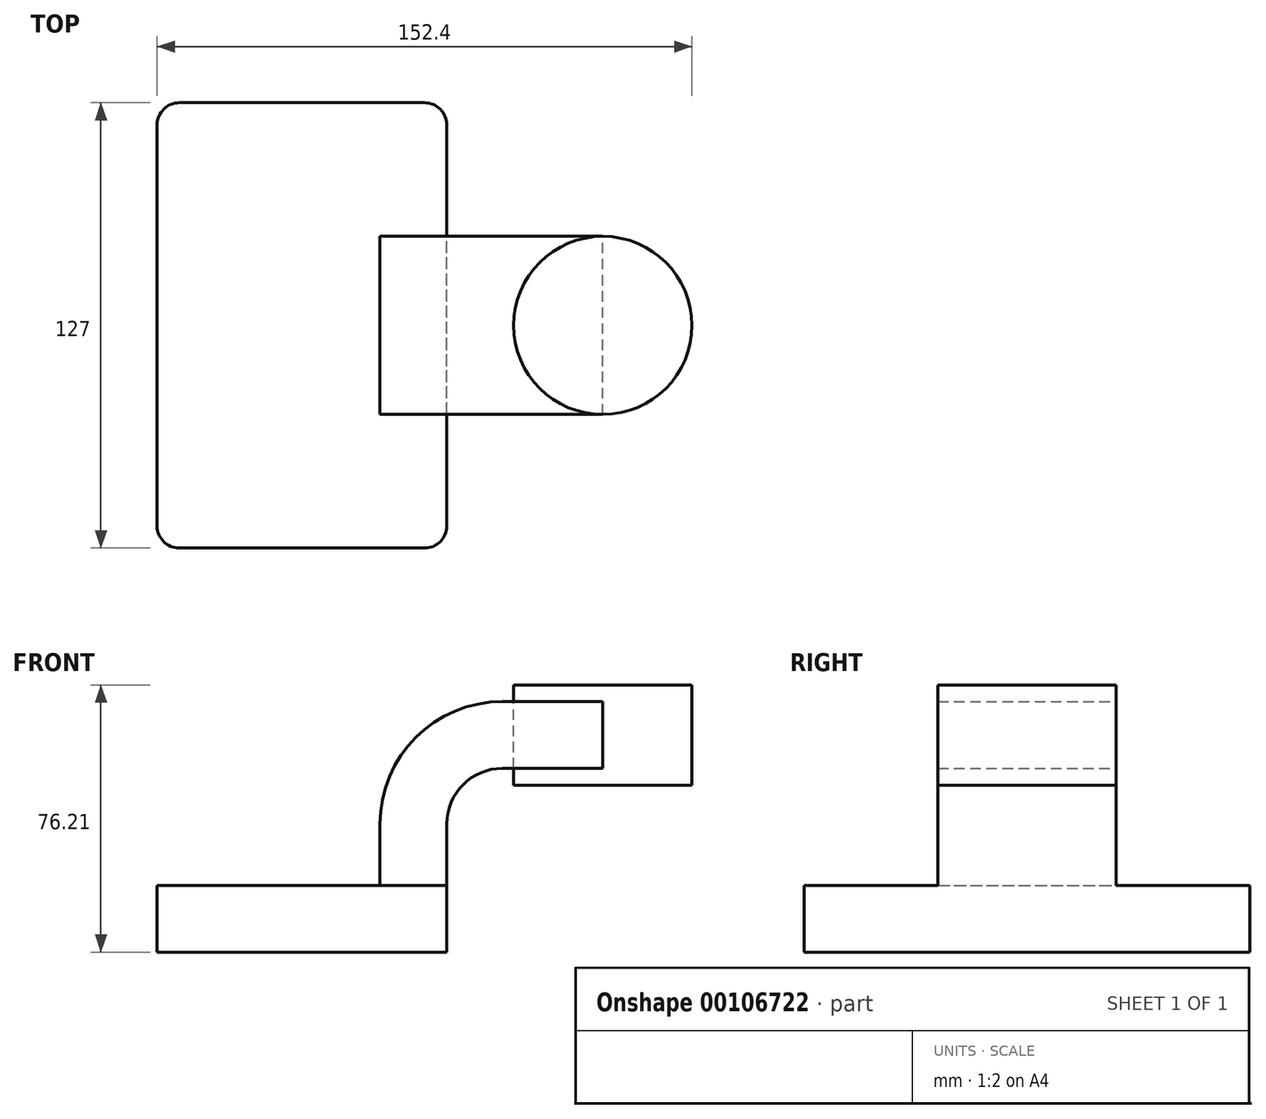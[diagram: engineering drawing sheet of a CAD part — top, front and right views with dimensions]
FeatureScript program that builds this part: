
annotation { "Feature Type Name" : "Feature", "Feature Type Description" : "" }
export const myFeature = defineFeature(function(context is Context, id is Id, definition is map)
    precondition{}
    {
        {
            var Q0;
            Q0=qCreatedBy(makeId("Front.planeOp"),FACE);
            var sketch = newSketch(context, id + "F0", { "sketchPlane" : qUnion([Q0])});
            skLineSegment(sketch, "E0.bottom", {"start": v(41.27, 9.53) * mm, "end": v(-41.28, 9.53) * mm});
            skLineSegment(sketch, "E0.top", {"start": v(41.28, -9.52) * mm, "end": v(-41.27, -9.52) * mm});
            skLineSegment(sketch, "E0.left", {"start": v(41.28, 9.53) * mm, "end": v(41.28, -9.52) * mm});
            skLineSegment(sketch, "E0.right", {"start": v(-41.28, 9.53) * mm, "end": v(-41.28, -9.52) * mm});
            skPoint(sketch, "E0.middle", {"position": v(0, 0) * mm});
            skLineSegment(sketch, "E1.bottom", {"start": v(60.32, 38.1) * mm, "end": v(111.12, 38.1) * mm});
            skLineSegment(sketch, "E1.top", {"start": v(60.32, 66.68) * mm, "end": v(111.12, 66.68) * mm});
            skLineSegment(sketch, "E1.left", {"start": v(60.32, 38.1) * mm, "end": v(60.32, 66.68) * mm});
            skLineSegment(sketch, "E1.right", {"start": v(111.12, 38.1) * mm, "end": v(111.12, 66.68) * mm});
            skPoint(sketch, "E1.middle", {"position": v(85.72, 52.39) * mm});
            skLineSegment(sketch, "E2", {"start": v(41.27, 9.53) * mm, "end": v(41.27, 27) * mm});
            skArc(sketch, "E3", {"start": v(41.27, 27) * mm, "mid": v(45.92, 38.23) * mm, "end": v(57.15, 42.88) * mm});
            skLineSegment(sketch, "E4", {"start": v(57.15, 42.88) * mm, "end": v(85.72, 42.88) * mm});
            skLineSegment(sketch, "E5.0", {"start": v(57.15, 61.93) * mm, "end": v(85.72, 61.93) * mm});
            skArc(sketch, "E5.1", {"start": v(22.22, 27) * mm, "mid": v(32.45, 51.7) * mm, "end": v(57.15, 61.93) * mm});
            skLineSegment(sketch, "E5.2", {"start": v(22.22, 9.53) * mm, "end": v(22.22, 27) * mm});
            skLineSegment(sketch, "E6", {"start": v(85.72, 61.93) * mm, "end": v(85.72, 42.88) * mm});
            skFitSpline(sketch, "E7", {"points": [v(-41.28, 9.53) * mm, v(57.15, 61.93) * mm], "startDerivative": vector(0.53, 82.1) * mm, "endDerivative": vector(135.42, -0.41) * mm});
            skPoint(sketch, "E8", {"position": v(85.72, 66.68) * mm});
            skLineSegment(sketch, "E9", {"start": v(85.72, 66.68) * mm, "end": v(85.72, 38.1) * mm});
            skSolve(sketch);
        }
        {
            var Q0;
            Q0=makeQuery(id+"F0.imprint","IMPRINT",FACE,{"disambiguationData":[TD([[makeQuery(id+"F0.imprint","IMPRINT",EDGE,{"derivedFrom":sQuery(id+"F0.wireOp",EDGE,"E0.top")}),-1.0]])]});
            extrude(context, id + "F1", {"entities" : qUnion([Q0]), "endBound" : BoundingType.SYMMETRIC, "depth" : 127 * mm});
        }
        {
            var Q0;
            {var subQ1=sQuery(id+"F0.wireOp",EDGE,"E2");Q0=makeQuery(id+"F0.imprint","IMPRINT",FACE,{"disambiguationData":[TD([[makeQuery(id+"F0.imprint","IMPRINT",EDGE,{"derivedFrom":subQ1}),1.0]])]});}
            var Q1;
            {var subQ5=sQuery(id+"F0.wireOp",EDGE,"E6");Q1=makeQuery(id+"F0.imprint","IMPRINT",FACE,{"disambiguationData":[TD([[makeQuery(id+"F0.imprint","IMPRINT",EDGE,{"derivedFrom":subQ5}),-1.0]])]});}
            var Q2;
            {var subQ0=sQuery(id+"F0.wireOp",EDGE,"E4");var subQ1=sQuery(id+"F0.wireOp",EDGE,"E1.left");var subQ2=makeQuery(id+"F0.imprint","INTERSECT",VERTEX,{"derivedFrom":[subQ1,subQ0]});Q2=makeQuery(id+"F0.imprint","IMPRINT",FACE,{"disambiguationData":[TD([[makeQuery(id+"F0.imprint","IMPRINT",EDGE,{"disambiguationData":[TD([[subQ2,-1.0]])],"derivedFrom":subQ1}),-1.0]])]});}
            extrude(context, id + "F2", {"entities" : qUnion([Q0, Q1, Q2]), "operationType" : NewBodyOperationType.ADD, "endBound" : BoundingType.SYMMETRIC, "depth" : 50.8 * mm});
        }
        {
            var Q0;
            Q0=makeQuery(id+"F0.imprint","IMPRINT",FACE,{"disambiguationData":[TD([[makeQuery(id+"F0.imprint","IMPRINT",EDGE,{"derivedFrom":sQuery(id+"F0.wireOp",EDGE,"E5.1")}),1.0]])]});
            extrude(context, id + "F3", {"entities" : qUnion([Q0]), "operationType" : NewBodyOperationType.ADD, "endBound" : BoundingType.SYMMETRIC, "depth" : 15.88 * mm});
        }
        {
            var Q0;
            {var subQ0=sQuery(id+"F0.wireOp",EDGE,"E1.right");Q0=makeQuery(id+"F0.imprint","IMPRINT",FACE,{"disambiguationData":[TD([[makeQuery(id+"F0.imprint","IMPRINT",EDGE,{"derivedFrom":subQ0}),1.0]])]});}
            var Q1;
            Q1=sQuery(id+"F0.wireOp",EDGE,"E9");
            revolve(context, id + "F4", {"entities" : qUnion([Q0]), "axis" : qUnion([Q1]), "revolveType" : RevolveType.FULL});
        }
        {
            var Q0;
            Q0=makeQuery(id+"F1.opExtrude","CAP_EDGE",EDGE,{"disambiguationData":[OSD([sQuery(id+"F0.wireOp",EDGE,"E0.left")])],"isStart":false});
            var Q1;
            Q1=makeQuery(id+"F1.opExtrude","CAP_EDGE",EDGE,{"disambiguationData":[OSD([sQuery(id+"F0.wireOp",EDGE,"E0.right")])],"isStart":false});
            var Q2;
            Q2=makeQuery(id+"F1.opExtrude","CAP_EDGE",EDGE,{"disambiguationData":[OSD([sQuery(id+"F0.wireOp",EDGE,"E0.left")])],"isStart":true});
            var Q3;
            Q3=makeQuery(id+"F1.opExtrude","CAP_EDGE",EDGE,{"disambiguationData":[OSD([sQuery(id+"F0.wireOp",EDGE,"E0.right")])],"isStart":true});
            fillet(context, id + "F5", {"entities" : qUnion([Q0, Q1, Q2, Q3]), "radius" : 6.35 * mm, "tangentPropagation" : true, "allowEdgeOverflow" : false});
        }
    });
